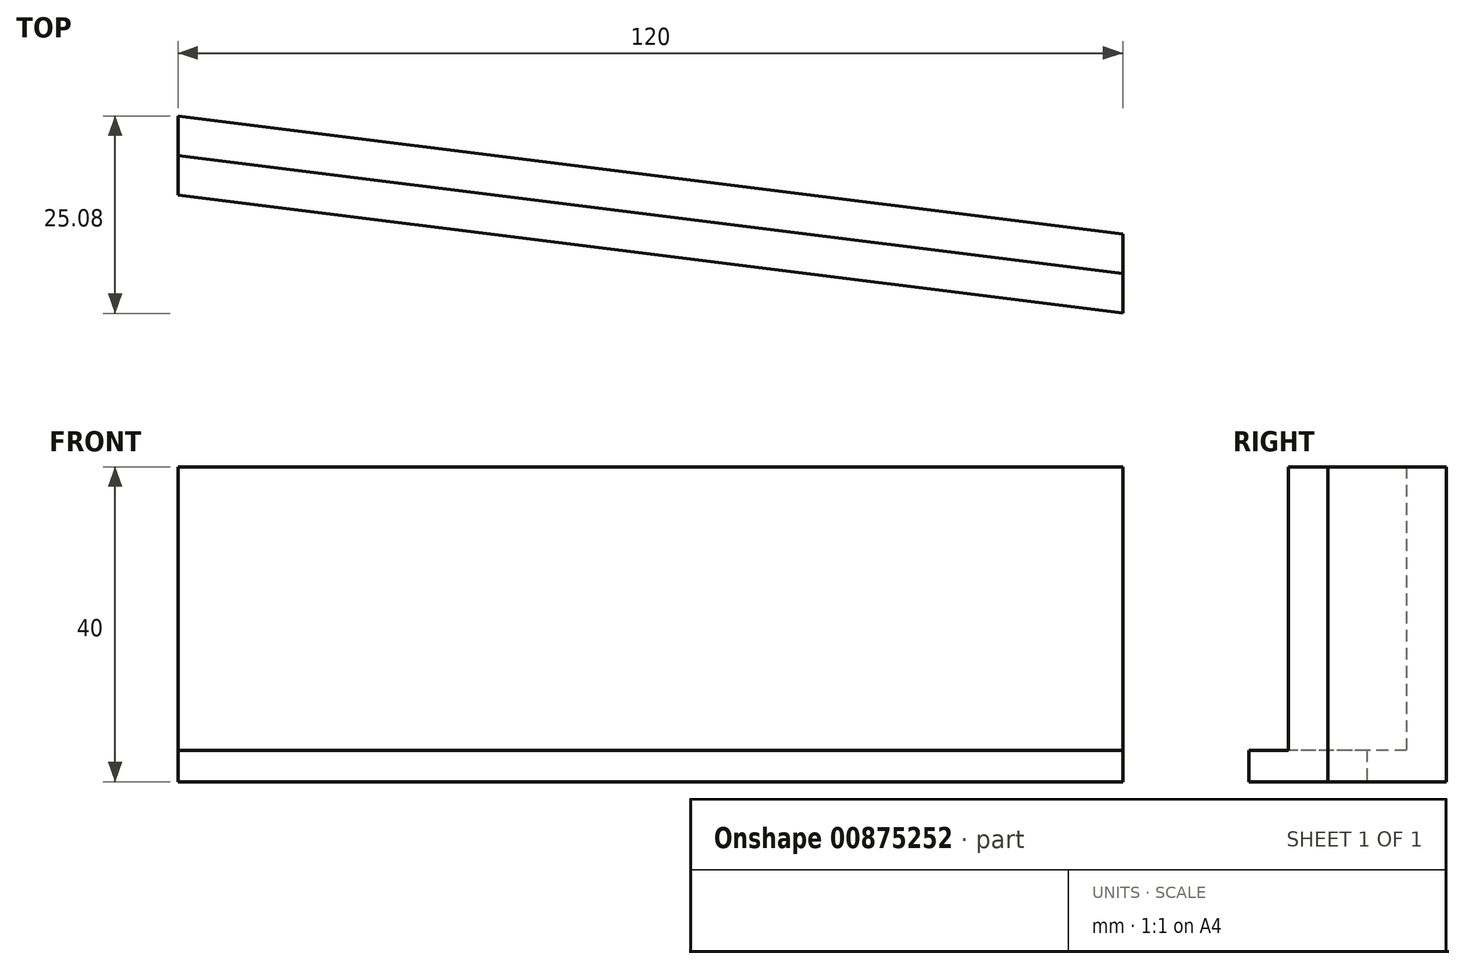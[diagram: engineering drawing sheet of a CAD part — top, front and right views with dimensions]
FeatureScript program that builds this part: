
annotation { "Feature Type Name" : "Feature", "Feature Type Description" : "" }
export const myFeature = defineFeature(function(context is Context, id is Id, definition is map)
    precondition{}
    {
        {
            var Q0;
            Q0=qCreatedBy(makeId("Top.planeOp"),FACE);
            var sketch = newSketch(context, id + "F0", { "sketchPlane" : qUnion([Q0])});
            skLineSegment(sketch, "E0", {"start": v(0, 0) * mm, "end": v(0, -60) * mm, "construction": true});
            skLineSegment(sketch, "E1", {"start": v(0, -60) * mm, "end": v(120, -60) * mm, "construction": true});
            skLineSegment(sketch, "E2", {"start": v(120, -60) * mm, "end": v(120, -15) * mm, "construction": true});
            skLineSegment(sketch, "E3", {"start": v(120, -15) * mm, "end": v(0, 0) * mm});
            skLineSegment(sketch, "E4", {"start": v(0, -5.04) * mm, "end": v(120, -20.04) * mm});
            skLineSegment(sketch, "E5", {"start": v(0, 0) * mm, "end": v(0, -5.04) * mm});
            skLineSegment(sketch, "E6", {"start": v(120, -15) * mm, "end": v(120, -20.04) * mm});
            skSolve(sketch);
        }
        {
            var Q0;
            Q0=qSketchRegion(id+"F0",true);
            extrude(context, id + "F1", {"entities" : qUnion([Q0]), "depth" : 40 * mm, "offsetDistance" : 25 * mm});
        }
        {
            var Q0;
            Q0=makeQuery(id+"F1.opExtrude","CAP_FACE",FACE,{"disambiguationData":[OSD([sQuery(id+"F0.wireOp",EDGE,"E3"),sQuery(id+"F0.wireOp",EDGE,"E4"),sQuery(id+"F0.wireOp",EDGE,"E5"),sQuery(id+"F0.wireOp",EDGE,"E6")])],"isStart":true});
            var sketch = newSketch(context, id + "F2", { "sketchPlane" : qUnion([Q0])});
            skLineSegment(sketch, "E7.0", {"start": v(0, 5.04) * mm, "end": v(120, 20.04) * mm});
            skLineSegment(sketch, "E8", {"start": v(0, 5.04) * mm, "end": v(0, 10.08) * mm});
            skLineSegment(sketch, "E9", {"start": v(0, 10.08) * mm, "end": v(120, 25.08) * mm});
            skLineSegment(sketch, "E10", {"start": v(120, 25.08) * mm, "end": v(120, 20.04) * mm});
            skSolve(sketch);
        }
        {
            var Q0;
            Q0=qSketchRegion(id+"F2",true);
            extrude(context, id + "F3", {"entities" : qUnion([Q0]), "operationType" : NewBodyOperationType.ADD, "oppositeDirection" : true, "depth" : 4 * mm, "offsetDistance" : 25 * mm});
        }
    });
